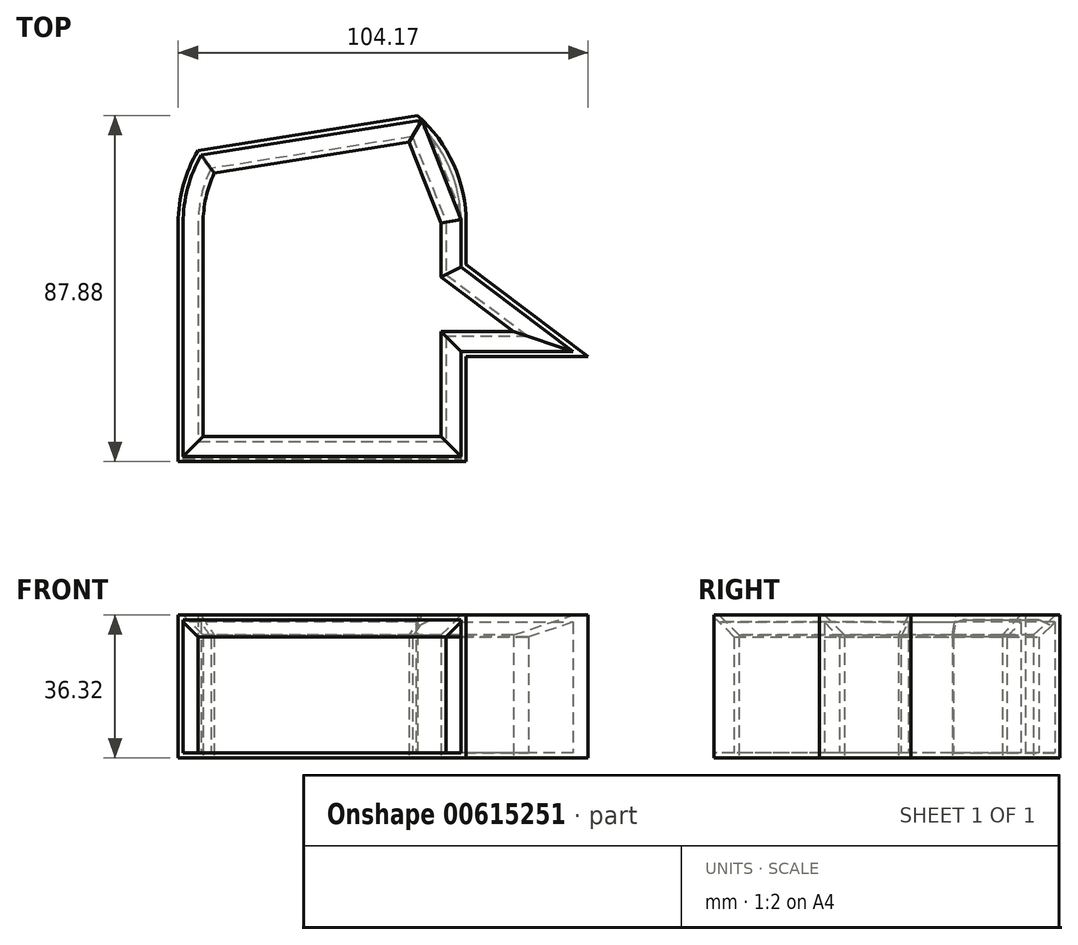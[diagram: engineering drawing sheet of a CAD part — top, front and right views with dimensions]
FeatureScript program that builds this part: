
annotation { "Feature Type Name" : "Feature", "Feature Type Description" : "" }
export const myFeature = defineFeature(function(context is Context, id is Id, definition is map)
    precondition{}
    {
        {
            var Q0;
            Q0=qCreatedBy(makeId("Top.planeOp"),FACE);
            var sketch = newSketch(context, id + "F0", { "sketchPlane" : qUnion([Q0])});
            skLineSegment(sketch, "E0.top", {"start": v(-31.07, -26.72) * mm, "end": v(29.4, -26.72) * mm});
            skLineSegment(sketch, "E0.left", {"start": v(-31.07, 27.45) * mm, "end": v(-31.07, -26.72) * mm});
            skLineSegment(sketch, "E0.right", {"start": v(29.4, 27.45) * mm, "end": v(29.4, 13.79) * mm});
            skLineSegment(sketch, "E1", {"start": v(29.4, 13.79) * mm, "end": v(47.74, 0) * mm});
            skLineSegment(sketch, "E2", {"start": v(21.3, 48.04) * mm, "end": v(-28.25, 40.2) * mm});
            skArc(sketch, "E3.trimOffspring", {"start": v(-28.25, 40.2) * mm, "mid": v(-30.36, 33.98) * mm, "end": v(-31.07, 27.45) * mm});
            skLineSegment(sketch, "E4", {"start": v(47.74, 0) * mm, "end": v(29.4, 0) * mm});
            skLineSegment(sketch, "E5.trimOffspring", {"start": v(29.4, 0) * mm, "end": v(29.4, -26.72) * mm});
            skArc(sketch, "E6.0", {"start": v(35.75, 27.45) * mm, "mid": v(32.53, 42.45) * mm, "end": v(23.44, 54.81) * mm});
            skLineSegment(sketch, "E6.1", {"start": v(35.75, 27.45) * mm, "end": v(35.75, 16.96) * mm});
            skLineSegment(sketch, "E6.2", {"start": v(23.44, 54.81) * mm, "end": v(-32.38, 45.97) * mm});
            skLineSegment(sketch, "E6.3", {"start": v(35.75, 16.96) * mm, "end": v(66.75, -6.35) * mm});
            skLineSegment(sketch, "E6.4", {"start": v(66.75, -6.35) * mm, "end": v(35.75, -6.35) * mm});
            skArc(sketch, "E6.5", {"start": v(-32.38, 45.97) * mm, "mid": v(-36.14, 37.05) * mm, "end": v(-37.42, 27.45) * mm});
            skLineSegment(sketch, "E6.6", {"start": v(-37.42, 27.45) * mm, "end": v(-37.42, -33.07) * mm});
            skLineSegment(sketch, "E6.7", {"start": v(-37.42, -33.07) * mm, "end": v(35.75, -33.07) * mm});
            skLineSegment(sketch, "E6.8", {"start": v(35.75, -6.35) * mm, "end": v(35.75, -33.07) * mm});
            skLineSegment(sketch, "E7.0", {"start": v(20.3, 54.31) * mm, "end": v(-29.24, 46.47) * mm});
            skLineSegment(sketch, "E8", {"start": v(21.3, 48.04) * mm, "end": v(29.4, 27.45) * mm});
            skSolve(sketch);
        }
        {
            var Q0;
            Q0=makeQuery(id+"F0.imprint","IMPRINT",FACE,{"disambiguationData":[TD([[makeQuery(id+"F0.imprint","IMPRINT",EDGE,{"derivedFrom":sQuery(id+"F0.wireOp",EDGE,"E0.top")}),-1.0]])]});
            extrude(context, id + "F1", {"entities" : qUnion([Q0]), "endBound" : BoundingType.SYMMETRIC, "depth" : 36.32 * mm, "offsetDistance" : 25.4 * mm});
        }
        {
            var Q0;
            Q0=makeQuery(id+"F1.opExtrude","CAP_EDGE",EDGE,{"disambiguationData":[OSD([sQuery(id+"F0.wireOp",EDGE,"E0.left")])],"isStart":false});
            var Q1;
            Q1=makeQuery(id+"F1.opExtrude","CAP_EDGE",EDGE,{"disambiguationData":[OSD([sQuery(id+"F0.wireOp",EDGE,"E2")])],"isStart":false});
            var Q2;
            Q2=makeQuery(id+"F1.opExtrude","CAP_EDGE",EDGE,{"disambiguationData":[OSD([sQuery(id+"F0.wireOp",EDGE,"E8")])],"isStart":false});
            var Q3;
            Q3=makeQuery(id+"F1.opExtrude","CAP_EDGE",EDGE,{"disambiguationData":[OSD([sQuery(id+"F0.wireOp",EDGE,"E0.right")])],"isStart":false});
            var Q4;
            Q4=makeQuery(id+"F1.opExtrude","CAP_EDGE",EDGE,{"disambiguationData":[OSD([sQuery(id+"F0.wireOp",EDGE,"E1")])],"isStart":false});
            var Q5;
            Q5=makeQuery(id+"F1.opExtrude","CAP_EDGE",EDGE,{"disambiguationData":[OSD([sQuery(id+"F0.wireOp",EDGE,"E4")])],"isStart":false});
            var Q6;
            Q6=makeQuery(id+"F1.opExtrude","CAP_EDGE",EDGE,{"disambiguationData":[OSD([sQuery(id+"F0.wireOp",EDGE,"E5.trimOffspring")])],"isStart":false});
            var Q7;
            Q7=makeQuery(id+"F1.opExtrude","CAP_EDGE",EDGE,{"disambiguationData":[OSD([sQuery(id+"F0.wireOp",EDGE,"E0.top")])],"isStart":false});
            chamfer(context, id + "F2", {"entities" : qUnion([Q0, Q1, Q2, Q3, Q4, Q5, Q6, Q7]), "width" : 5.08 * mm, "tangentPropagation" : true});
        }
        {
            var Q0;
            Q0=makeQuery(id+"F1.opExtrude","SWEPT_FACE",FACE,{"disambiguationData":[OSD([sQuery(id+"F0.wireOp",EDGE,"E6.7")])]});
            shell(context, id + "F3", {"entities" : qUnion([Q0]), "thickness" : 1.27 * mm});
        }
    });
